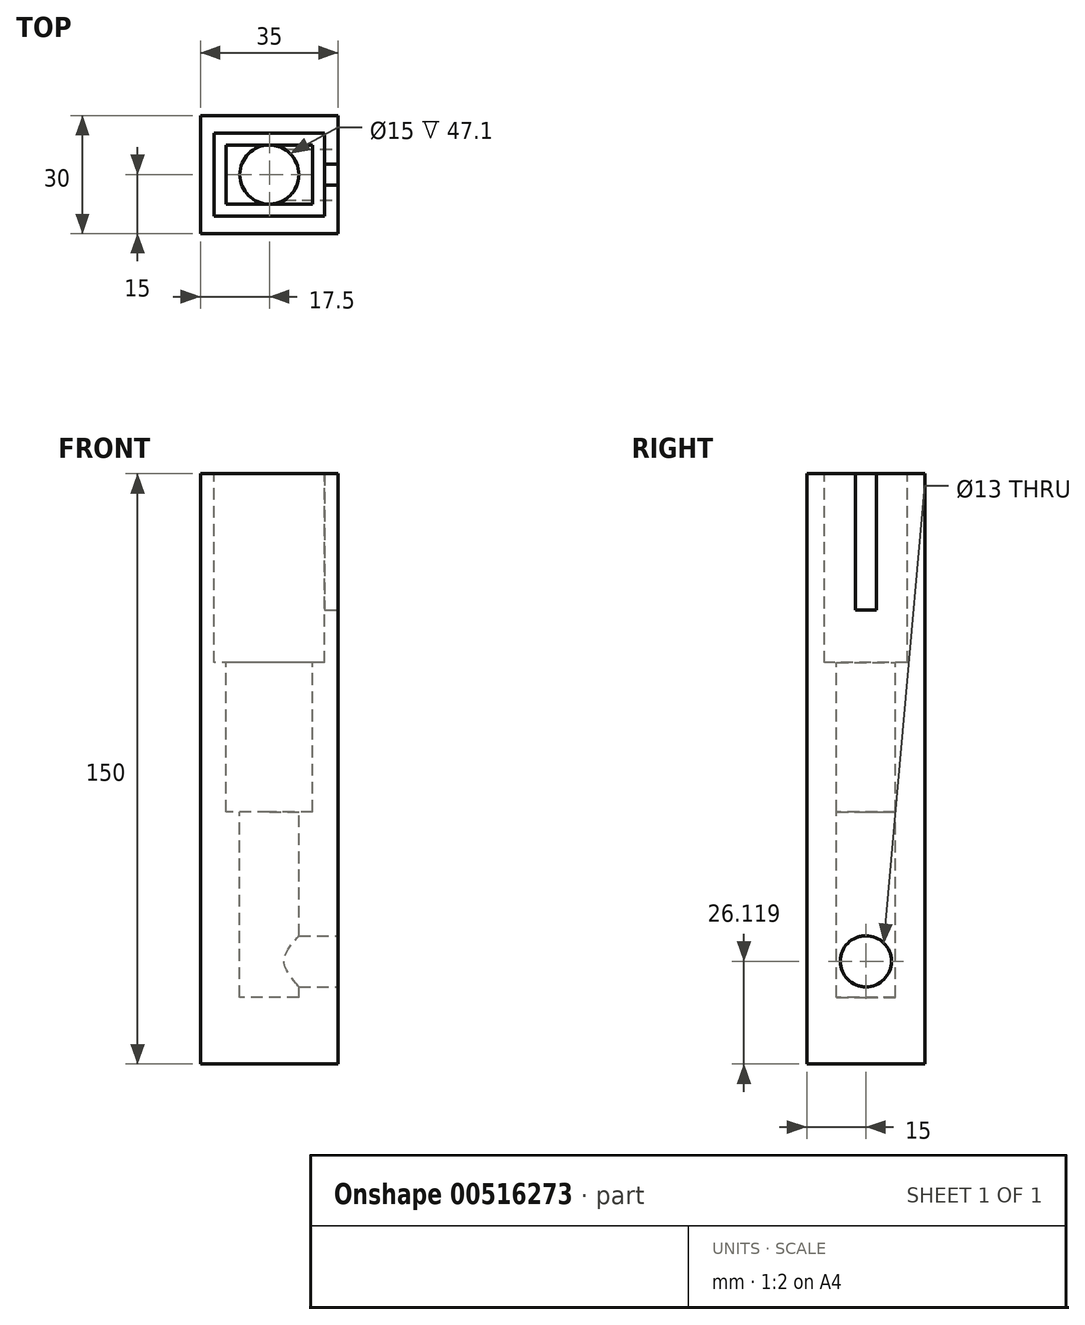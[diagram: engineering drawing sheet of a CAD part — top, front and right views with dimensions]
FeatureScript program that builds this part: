
annotation { "Feature Type Name" : "Feature", "Feature Type Description" : "" }
export const myFeature = defineFeature(function(context is Context, id is Id, definition is map)
    precondition{}
    {
        {
            var Q0;
            Q0=qCreatedBy(makeId("Top.planeOp"),FACE);
            var sketch = newSketch(context, id + "F0", { "sketchPlane" : qUnion([Q0])});
            skLineSegment(sketch, "E0.bottom", {"start": v(17.5, 15) * mm, "end": v(-17.5, 15) * mm});
            skLineSegment(sketch, "E0.top", {"start": v(17.5, -15) * mm, "end": v(-17.5, -15) * mm});
            skLineSegment(sketch, "E0.left", {"start": v(17.5, 15) * mm, "end": v(17.5, -15) * mm});
            skLineSegment(sketch, "E0.right", {"start": v(-17.5, 15) * mm, "end": v(-17.5, -15) * mm});
            skPoint(sketch, "E0.middle", {"position": v(0, 0) * mm});
            skSolve(sketch);
        }
        {
            var Q0;
            Q0=makeQuery(id+"F0.imprint","IMPRINT",FACE,{"disambiguationData":[TD([[makeQuery(id+"F0.imprint","IMPRINT",EDGE,{"derivedFrom":sQuery(id+"F0.wireOp",EDGE,"E0.bottom")}),1.0]])]});
            extrude(context, id + "F1", {"entities" : qUnion([Q0]), "depth" : 150 * mm});
        }
        {
            var Q0;
            Q0=makeQuery(id+"F1.opExtrude","CAP_FACE",FACE,{"disambiguationData":[OSD([sQuery(id+"F0.wireOp",EDGE,"E0.bottom"),sQuery(id+"F0.wireOp",EDGE,"E0.top"),sQuery(id+"F0.wireOp",EDGE,"E0.left"),sQuery(id+"F0.wireOp",EDGE,"E0.right")])],"isStart":false});
            var sketch = newSketch(context, id + "F2", { "sketchPlane" : qUnion([Q0])});
            skLineSegment(sketch, "E1.bottom", {"start": v(14, 10.5) * mm, "end": v(-14, 10.5) * mm});
            skLineSegment(sketch, "E1.top", {"start": v(14, -10.5) * mm, "end": v(-14, -10.5) * mm});
            skLineSegment(sketch, "E1.left", {"start": v(14, 10.5) * mm, "end": v(14, -10.5) * mm});
            skLineSegment(sketch, "E1.right", {"start": v(-14, 10.5) * mm, "end": v(-14, -10.5) * mm});
            skPoint(sketch, "E1.middle", {"position": v(0, 0) * mm});
            skSolve(sketch);
        }
        {
            var Q0;
            Q0=qSketchRegion(id+"F2",true);
            extrude(context, id + "F3", {"entities" : qUnion([Q0]), "operationType" : NewBodyOperationType.REMOVE, "oppositeDirection" : true, "depth" : 48 * mm});
        }
        {
            var Q0;
            Q0=makeQuery(id+"F2.imprint","IMPRINT",FACE,{"disambiguationData":[TD([[makeQuery(id+"F2.imprint","IMPRINT",EDGE,{"derivedFrom":sQuery(id+"F2.wireOp",EDGE,"E1.bottom")}),1.0]])]});
            var sketch = newSketch(context, id + "F4", { "sketchPlane" : qUnion([Q0])});
            skLineSegment(sketch, "E2.bottom", {"start": v(11, -7.5) * mm, "end": v(-11, -7.5) * mm});
            skLineSegment(sketch, "E2.top", {"start": v(11, 7.5) * mm, "end": v(-11, 7.5) * mm});
            skLineSegment(sketch, "E2.left", {"start": v(11, -7.5) * mm, "end": v(11, 7.5) * mm});
            skLineSegment(sketch, "E2.right", {"start": v(-11, -7.5) * mm, "end": v(-11, 7.5) * mm});
            skPoint(sketch, "E2.middle", {"position": v(0, 0) * mm});
            skSolve(sketch);
        }
        {
            var Q0;
            Q0=qSketchRegion(id+"F4",true);
            extrude(context, id + "F5", {"entities" : qUnion([Q0]), "operationType" : NewBodyOperationType.REMOVE, "oppositeDirection" : true, "depth" : 85.9 * mm});
        }
        {
            var Q0;
            Q0=makeQuery(id+"F1.opExtrude","SWEPT_FACE",FACE,{"disambiguationData":[OSD([sQuery(id+"F0.wireOp",EDGE,"E0.left")])]});
            var sketch = newSketch(context, id + "F6", { "sketchPlane" : qUnion([Q0])});
            skCircle(sketch, "E3", {"center": v(0, 26.12) * mm, "radius": 6.5 * mm});
            skSolve(sketch);
        }
        {
            var Q0;
            Q0=makeQuery(id+"F6.imprint","IMPRINT",FACE,{"disambiguationData":[TD([[makeQuery(id+"F6.imprint","IMPRINT",EDGE,{"derivedFrom":sQuery(id+"F6.wireOp",EDGE,"E3")}),1.0]])]});
            extrude(context, id + "F7", {"entities" : qUnion([Q0]), "operationType" : NewBodyOperationType.REMOVE, "oppositeDirection" : true, "depth" : 15 * mm});
        }
        {
            var Q0;
            Q0=makeQuery(id+"F1.opExtrude","SWEPT_FACE",FACE,{"disambiguationData":[OSD([sQuery(id+"F0.wireOp",EDGE,"E0.left")])]});
            var sketch = newSketch(context, id + "F8", { "sketchPlane" : qUnion([Q0])});
            skSolve(sketch);
        }
        {
            var Q0;
            {var subQ0=sQuery(id+"F0.wireOp",EDGE,"E0.left");Q0=makeQuery(id+"F8.imprint","IMPRINT",FACE,{"disambiguationData":[TD([[makeQuery(id+"F8.imprint","IMPRINT",EDGE,{"derivedFrom":makeQuery(id+"F1.opExtrude","CAP_EDGE",EDGE,{"disambiguationData":[OSD([subQ0])],"isStart":true})}),-1.0]])]});}
            var sketch = newSketch(context, id + "F9", { "sketchPlane" : qUnion([Q0])});
            skLineSegment(sketch, "E4.bottom", {"start": v(2.7, 115.37) * mm, "end": v(-2.7, 115.37) * mm});
            skLineSegment(sketch, "E4.top", {"start": v(2.7, 185.34) * mm, "end": v(-2.7, 185.34) * mm});
            skLineSegment(sketch, "E4.left", {"start": v(2.7, 115.37) * mm, "end": v(2.7, 185.34) * mm});
            skLineSegment(sketch, "E4.right", {"start": v(-2.7, 115.37) * mm, "end": v(-2.7, 185.34) * mm});
            skPoint(sketch, "E4.middle", {"position": v(0, 150.35) * mm});
            skSolve(sketch);
        }
        {
            var Q0;
            Q0=qSketchRegion(id+"F9",true);
            extrude(context, id + "F10", {"entities" : qUnion([Q0]), "operationType" : NewBodyOperationType.REMOVE, "oppositeDirection" : true, "depth" : 5 * mm});
        }
        {
            var Q0;
            Q0=makeQuery(id+"F2.imprint","IMPRINT",FACE,{"disambiguationData":[TD([[makeQuery(id+"F2.imprint","IMPRINT",EDGE,{"derivedFrom":sQuery(id+"F2.wireOp",EDGE,"E1.bottom")}),1.0]])]});
            var sketch = newSketch(context, id + "F11", { "sketchPlane" : qUnion([Q0])});
            skCircle(sketch, "E5", {"center": v(0, 0) * mm, "radius": 7.5 * mm});
            skSolve(sketch);
        }
        {
            var Q0;
            Q0=qSketchRegion(id+"F11",true);
            extrude(context, id + "F12", {"entities" : qUnion([Q0]), "operationType" : NewBodyOperationType.REMOVE, "oppositeDirection" : true, "depth" : 133 * mm});
        }
    });
